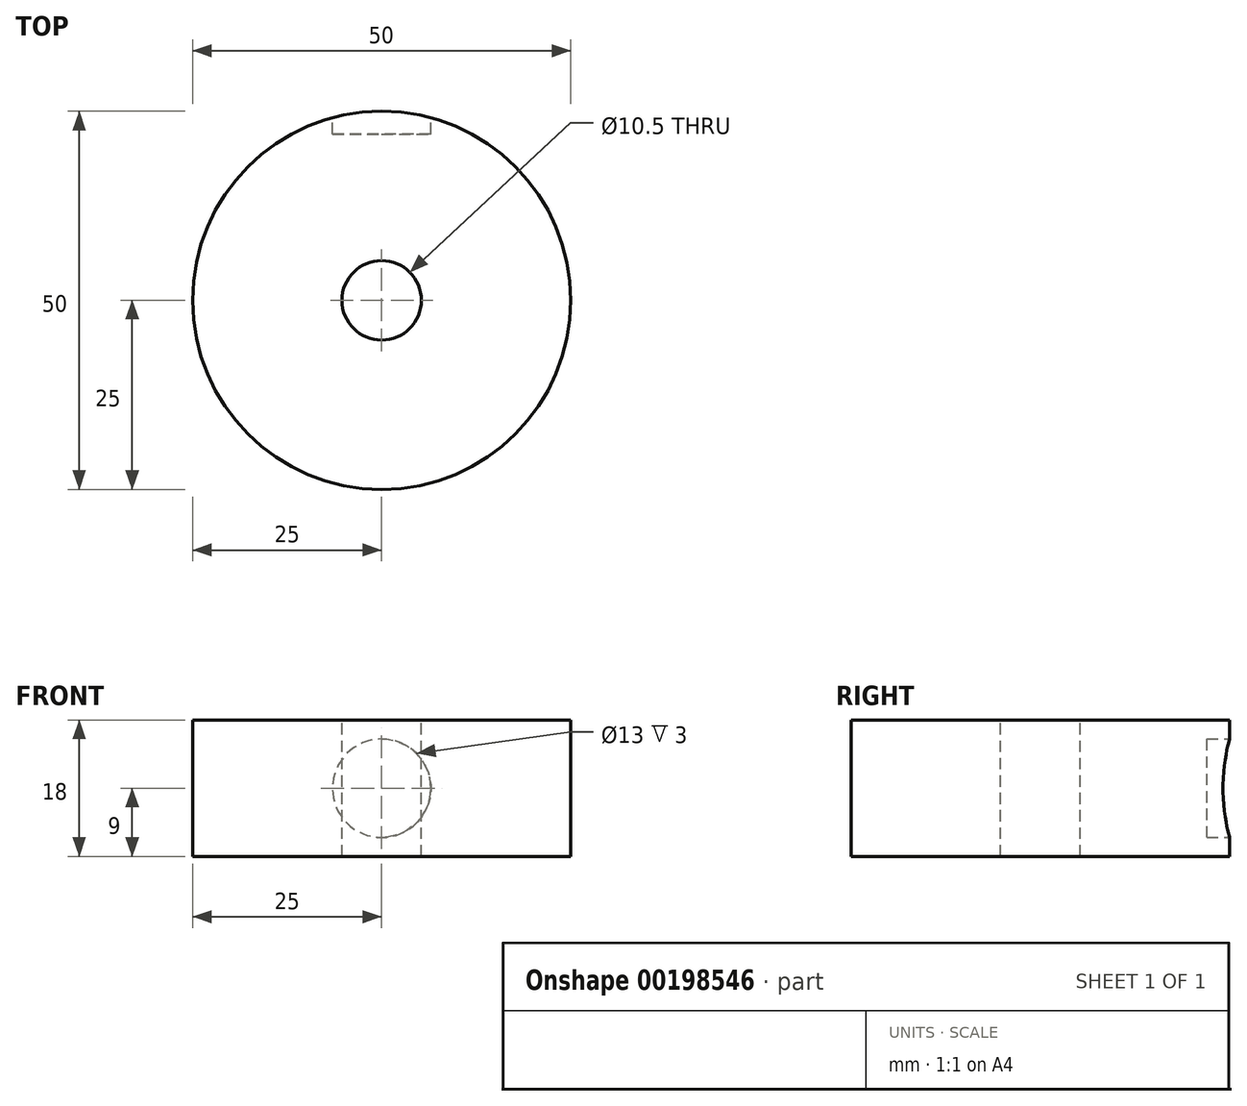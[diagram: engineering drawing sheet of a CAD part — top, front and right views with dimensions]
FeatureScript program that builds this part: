
annotation { "Feature Type Name" : "Feature", "Feature Type Description" : "" }
export const myFeature = defineFeature(function(context is Context, id is Id, definition is map)
    precondition{}
    {
        {
            var Q0;
            Q0=qCreatedBy(makeId("Front.planeOp"),FACE);
            var sketch = newSketch(context, id + "F0", { "sketchPlane" : qUnion([Q0])});
            skLineSegment(sketch, "E0.bottom", {"start": v(-25, 9) * mm, "end": v(25, 9) * mm});
            skLineSegment(sketch, "E0.top", {"start": v(-25, -9) * mm, "end": v(25, -9) * mm});
            skLineSegment(sketch, "E0.left", {"start": v(-25, 9) * mm, "end": v(-25, -9) * mm});
            skLineSegment(sketch, "E0.right", {"start": v(25, 9) * mm, "end": v(25, -9) * mm});
            skPoint(sketch, "E0.middle", {"position": v(0, 0) * mm});
            skCircle(sketch, "E1", {"center": v(0, 0) * mm, "radius": 6.5 * mm});
            skSolve(sketch);
        }
        {
            var Q0;
            Q0=makeQuery(id+"F0.imprint","IMPRINT",FACE,{"disambiguationData":[TD([[makeQuery(id+"F0.imprint","IMPRINT",EDGE,{"derivedFrom":sQuery(id+"F0.wireOp",EDGE,"E0.bottom")}),-1.0]])]});
            var Q1;
            Q1=makeQuery(id+"F0.imprint","IMPRINT",FACE,{"disambiguationData":[TD([[makeQuery(id+"F0.imprint","IMPRINT",EDGE,{"derivedFrom":sQuery(id+"F0.wireOp",EDGE,"E1")}),1.0]])]});
            extrude(context, id + "F1", {"entities" : qUnion([Q0, Q1]), "depth" : 50 * mm});
        }
        {
            var Q0;
            Q0=qCreatedBy(makeId("Front.planeOp"),FACE);
            var sketch = newSketch(context, id + "F2", { "sketchPlane" : qUnion([Q0])});
            skCircle(sketch, "E2", {"center": v(0, 0) * mm, "radius": 6.5 * mm});
            skSolve(sketch);
        }
        {
            var Q0;
            Q0=makeQuery(id+"F2.imprint","IMPRINT",FACE,{"disambiguationData":[TD([[makeQuery(id+"F2.imprint","IMPRINT",EDGE,{"derivedFrom":sQuery(id+"F2.wireOp",EDGE,"E2")}),1.0]])]});
            extrude(context, id + "F3", {"entities" : qUnion([Q0]), "operationType" : NewBodyOperationType.REMOVE, "depth" : 3 * mm});
        }
        {
            var Q0;
            Q0=makeQuery(id+"F1.opExtrude","CAP_EDGE",EDGE,{"disambiguationData":[OSD([sQuery(id+"F0.wireOp",EDGE,"E0.left")])],"isStart":true});
            var Q1;
            Q1=makeQuery(id+"F1.opExtrude","CAP_EDGE",EDGE,{"disambiguationData":[OSD([sQuery(id+"F0.wireOp",EDGE,"E0.right")])],"isStart":true});
            var Q2;
            Q2=makeQuery(id+"F1.opExtrude","CAP_EDGE",EDGE,{"disambiguationData":[OSD([sQuery(id+"F0.wireOp",EDGE,"E0.right")])],"isStart":false});
            var Q3;
            Q3=makeQuery(id+"F1.opExtrude","CAP_EDGE",EDGE,{"disambiguationData":[OSD([sQuery(id+"F0.wireOp",EDGE,"E0.left")])],"isStart":false});
            fillet(context, id + "F4", {"entities" : qUnion([Q0, Q1, Q2, Q3]), "radius" : 25 * mm, "tangentPropagation" : true, "allowEdgeOverflow" : false});
        }
        {
            var Q0;
            Q0=makeQuery(id+"F1.opExtrude","SWEPT_FACE",FACE,{"disambiguationData":[OSD([sQuery(id+"F0.wireOp",EDGE,"E0.bottom")])]});
            var sketch = newSketch(context, id + "F5", { "sketchPlane" : qUnion([Q0])});
            skCircle(sketch, "E3", {"center": v(0, -25) * mm, "radius": 5.25 * mm});
            skSolve(sketch);
        }
        {
            var Q0;
            Q0=makeQuery(id+"F5.imprint","IMPRINT",FACE,{"disambiguationData":[TD([[makeQuery(id+"F5.imprint","IMPRINT",EDGE,{"derivedFrom":sQuery(id+"F5.wireOp",EDGE,"E3")}),1.0]])]});
            extrude(context, id + "F6", {"entities" : qUnion([Q0]), "operationType" : NewBodyOperationType.REMOVE, "oppositeDirection" : true, "depth" : 25 * mm});
        }
    });
